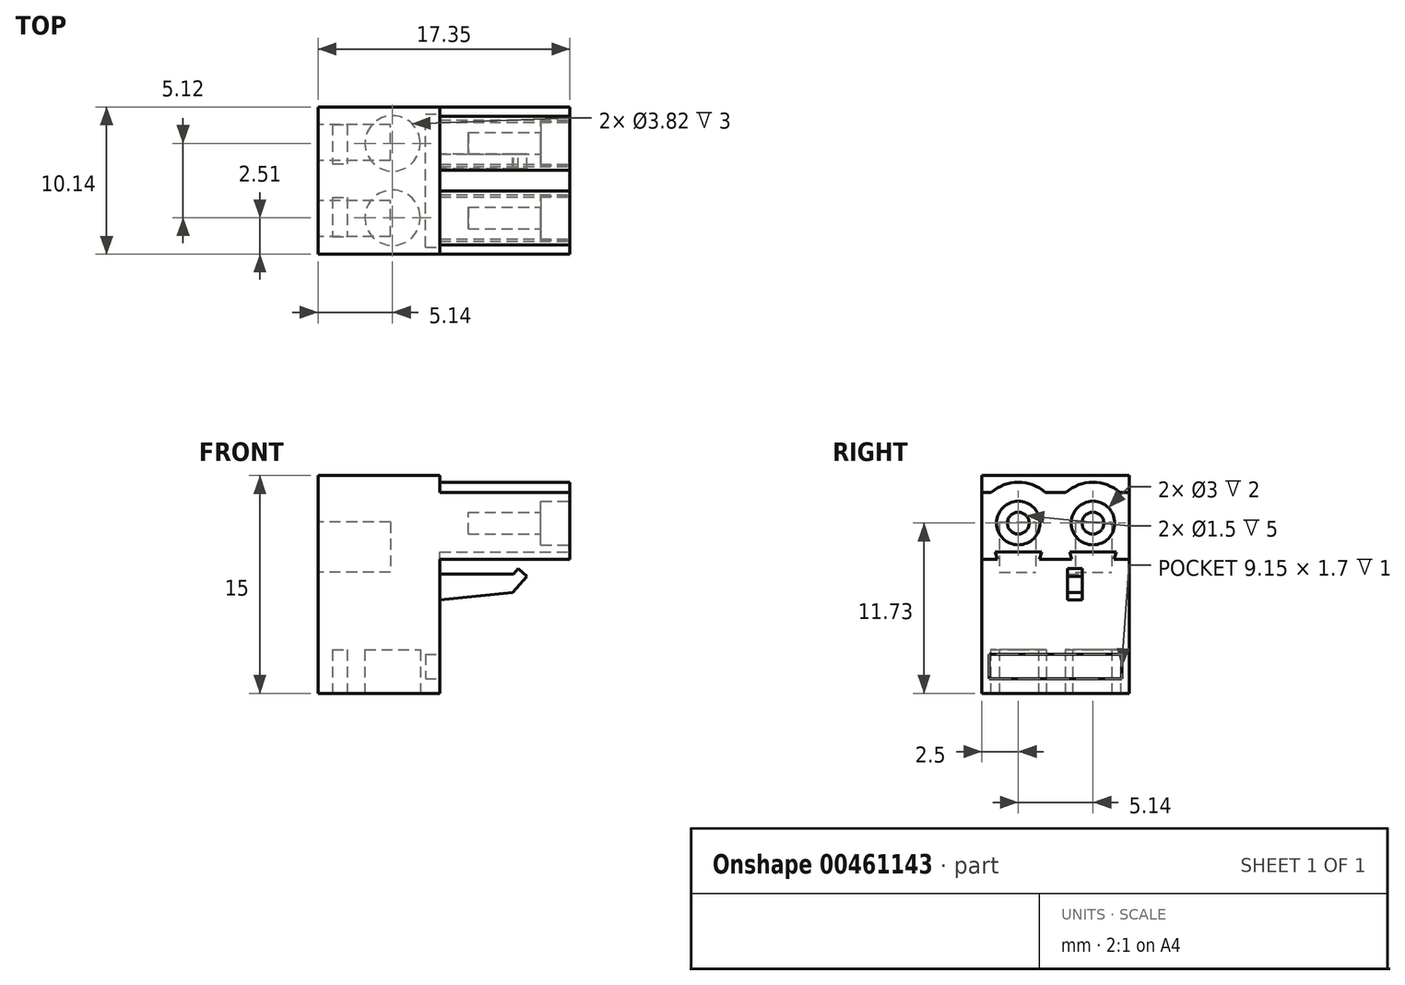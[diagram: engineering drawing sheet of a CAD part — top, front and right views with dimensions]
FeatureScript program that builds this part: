
annotation { "Feature Type Name" : "Feature", "Feature Type Description" : "" }
export const myFeature = defineFeature(function(context is Context, id is Id, definition is map)
    precondition{}
    {
        {
            var Q0;
            Q0=qCreatedBy(makeId("Front.planeOp"),FACE);
            var sketch = newSketch(context, id + "F0", { "sketchPlane" : qUnion([Q0])});
            skLineSegment(sketch, "E0", {"start": v(0, 15) * mm, "end": v(0, 0) * mm});
            skLineSegment(sketch, "E1", {"start": v(0, 0) * mm, "end": v(8.4, 0) * mm});
            skLineSegment(sketch, "E2", {"start": v(8.4, 0) * mm, "end": v(8.4, 9.23) * mm});
            skLineSegment(sketch, "E3", {"start": v(8.4, 9.23) * mm, "end": v(17.35, 9.23) * mm});
            skLineSegment(sketch, "E4", {"start": v(17.35, 9.23) * mm, "end": v(17.35, 13.83) * mm});
            skLineSegment(sketch, "E5", {"start": v(17.35, 13.83) * mm, "end": v(8.4, 13.83) * mm});
            skLineSegment(sketch, "E6", {"start": v(8.4, 13.83) * mm, "end": v(8.4, 15) * mm});
            skLineSegment(sketch, "E7", {"start": v(8.4, 15) * mm, "end": v(0, 15) * mm});
            skSolve(sketch);
        }
        {
            var Q0;
            Q0 = qSketchRegion(id + "F0", true);
            extrude(context, id + "F1", {"entities" : qUnion([Q0]), "depth" : 10.14 * mm});
        }
        {
            var Q0;
            Q0=makeQuery(id+"F1.opExtrude","SWEPT_FACE",FACE,{"disambiguationData":[OSD([sQuery(id+"F0.wireOp",EDGE,"E1")])]});
            var sketch = newSketch(context, id + "F2", { "sketchPlane" : qUnion([Q0])});
            skCircle(sketch, "E8", {"center": v(5.14, 2.5) * mm, "radius": 1.91 * mm});
            skCircle(sketch, "E9", {"center": v(5.14, 7.63) * mm, "radius": 1.91 * mm});
            skPoint(sketch, "E10", {"position": v(5.14, 9.54) * mm});
            skPoint(sketch, "E11", {"position": v(5.14, 0.6) * mm});
            skPoint(sketch, "E12", {"position": v(7.05, 2.5) * mm});
            skPoint(sketch, "E13", {"position": v(7.05, 7.63) * mm});
            skPoint(sketch, "E14", {"position": v(5.14, 4.42) * mm});
            skPoint(sketch, "E15", {"position": v(5.14, 5.72) * mm});
            skPoint(sketch, "E16", {"position": v(0, 0) * mm});
            skPoint(sketch, "E17", {"position": v(0, 10.14) * mm});
            skLineSegment(sketch, "E18.bottom", {"start": v(1, 1.2) * mm, "end": v(2, 1.2) * mm});
            skLineSegment(sketch, "E18.top", {"start": v(1, 3.9) * mm, "end": v(2, 3.9) * mm});
            skLineSegment(sketch, "E18.left", {"start": v(1, 1.2) * mm, "end": v(1, 3.9) * mm});
            skLineSegment(sketch, "E18.right", {"start": v(2, 1.2) * mm, "end": v(2, 3.9) * mm});
            skLineSegment(sketch, "E19.bottom", {"start": v(1, 6.24) * mm, "end": v(2, 6.24) * mm});
            skLineSegment(sketch, "E19.top", {"start": v(1, 8.94) * mm, "end": v(2, 8.94) * mm});
            skLineSegment(sketch, "E19.left", {"start": v(1, 6.24) * mm, "end": v(1, 8.94) * mm});
            skLineSegment(sketch, "E19.right", {"start": v(2, 6.24) * mm, "end": v(2, 8.94) * mm});
            skSolve(sketch);
        }
        {
            var Q0;
            Q0 = qSketchRegion(id + "F2", true);
            extrude(context, id + "F3", {"entities" : qUnion([Q0]), "operationType" : NewBodyOperationType.REMOVE, "oppositeDirection" : true, "depth" : 3 * mm});
        }
        {
            var Q0;
            Q0=makeQuery(id+"F1.opExtrude","SWEPT_FACE",FACE,{"disambiguationData":[OSD([sQuery(id+"F0.wireOp",EDGE,"E0")])]});
            var sketch = newSketch(context, id + "F4", { "sketchPlane" : qUnion([Q0])});
            skLineSegment(sketch, "E20.bottom", {"start": v(8.94, 11.8) * mm, "end": v(6.44, 11.8) * mm});
            skLineSegment(sketch, "E20.top", {"start": v(8.94, 8.35) * mm, "end": v(6.44, 8.35) * mm});
            skLineSegment(sketch, "E20.left", {"start": v(8.94, 11.8) * mm, "end": v(8.94, 8.35) * mm});
            skLineSegment(sketch, "E20.right", {"start": v(6.44, 11.8) * mm, "end": v(6.44, 8.35) * mm});
            skLineSegment(sketch, "E21.bottom", {"start": v(3.7, 11.8) * mm, "end": v(1.2, 11.8) * mm});
            skLineSegment(sketch, "E21.top", {"start": v(3.7, 8.35) * mm, "end": v(1.2, 8.35) * mm});
            skLineSegment(sketch, "E21.left", {"start": v(3.7, 11.8) * mm, "end": v(3.7, 8.35) * mm});
            skLineSegment(sketch, "E21.right", {"start": v(1.2, 11.8) * mm, "end": v(1.2, 8.35) * mm});
            skSolve(sketch);
        }
        {
            var Q0;
            Q0 = qSketchRegion(id + "F4", true);
            extrude(context, id + "F5", {"entities" : qUnion([Q0]), "operationType" : NewBodyOperationType.REMOVE, "oppositeDirection" : true, "depth" : 5 * mm});
        }
        {
            var Q0;
            Q0=makeQuery(id+"F1.opExtrude","SWEPT_FACE",FACE,{"disambiguationData":[OSD([sQuery(id+"F0.wireOp",EDGE,"E4")])]});
            var sketch = newSketch(context, id + "F6", { "sketchPlane" : qUnion([Q0])});
            skCircle(sketch, "E22", {"center": v(-2.5, 11.73) * mm, "radius": 1.5 * mm});
            skCircle(sketch, "E23", {"center": v(-7.64, 11.73) * mm, "radius": 1.5 * mm});
            skPoint(sketch, "E24", {"position": v(-2.5, 10.23) * mm});
            skPoint(sketch, "E25", {"position": v(-1, 11.73) * mm});
            skPoint(sketch, "E26", {"position": v(-6.14, 11.73) * mm});
            skPoint(sketch, "E27", {"position": v(-7.64, 10.23) * mm});
            skPoint(sketch, "E28", {"position": v(-9.14, 11.73) * mm});
            skSolve(sketch);
        }
        {
            var Q0;
            Q0 = qSketchRegion(id + "F6", true);
            extrude(context, id + "F7", {"entities" : qUnion([Q0]), "operationType" : NewBodyOperationType.REMOVE, "oppositeDirection" : true, "depth" : 2 * mm});
        }
        {
            var Q0;
            Q0=makeQuery(id+"F1.opExtrude","SWEPT_FACE",FACE,{"disambiguationData":[OSD([sQuery(id+"F0.wireOp",EDGE,"E4")])]});
            var sketch = newSketch(context, id + "F8", { "sketchPlane" : qUnion([Q0])});
            skLineSegment(sketch, "E29", {"start": v(-9.1, 9.23) * mm, "end": v(-9.25, 9.73) * mm});
            skLineSegment(sketch, "E30", {"start": v(-9.25, 9.73) * mm, "end": v(-6.03, 9.73) * mm});
            skLineSegment(sketch, "E31", {"start": v(-6.03, 9.73) * mm, "end": v(-6.2, 9.23) * mm});
            skLineSegment(sketch, "E32", {"start": v(-6.2, 9.23) * mm, "end": v(-9.1, 9.23) * mm});
            skLineSegment(sketch, "E33", {"start": v(-5.07, 9.23) * mm, "end": v(-5.07, 13.83) * mm, "construction": true});
            skLineSegment(sketch, "E34.MirrorCS", {"start": v(-0.9, 9.73) * mm, "end": v(-4.1, 9.73) * mm});
            skLineSegment(sketch, "E35.MirrorCS", {"start": v(-4.1, 9.73) * mm, "end": v(-3.95, 9.23) * mm});
            skLineSegment(sketch, "E36.MirrorCS", {"start": v(-3.95, 9.23) * mm, "end": v(-1.05, 9.23) * mm});
            skLineSegment(sketch, "E37.MirrorCS", {"start": v(-1.05, 9.23) * mm, "end": v(-0.9, 9.73) * mm});
            skPoint(sketch, "E38", {"position": v(-7.64, 9.23) * mm});
            skPoint(sketch, "E39", {"position": v(-7.64, 11.73) * mm});
            skLineSegment(sketch, "E40", {"start": v(-7.64, 11.73) * mm, "end": v(-7.64, 9.23) * mm});
            skSolve(sketch);
        }
        {
            var Q0;
            Q0 = qSketchRegion(id + "F8", true);
            extrude(context, id + "F9", {"entities" : qUnion([Q0]), "operationType" : NewBodyOperationType.REMOVE, "oppositeDirection" : true, "depth" : 8.95 * mm});
        }
        {
            var Q0;
            Q0=makeQuery(id+"F1.opExtrude","SWEPT_FACE",FACE,{"disambiguationData":[OSD([sQuery(id+"F0.wireOp",EDGE,"E4")])]});
            var sketch = newSketch(context, id + "F10", { "sketchPlane" : qUnion([Q0])});
            skPoint(sketch, "E41", {"position": v(-7.64, 11.73) * mm});
            skArc(sketch, "E42", {"start": v(-5.77, 13.83) * mm, "mid": v(-7.64, 14.54) * mm, "end": v(-9.5, 13.83) * mm});
            skLineSegment(sketch, "E43", {"start": v(-9.5, 13.83) * mm, "end": v(-5.77, 13.83) * mm});
            skPoint(sketch, "E44", {"position": v(-5.07, 13.83) * mm});
            skLineSegment(sketch, "E45", {"start": v(-5.07, 13.83) * mm, "end": v(-5.07, 9.23) * mm, "construction": true});
            skArc(sketch, "E46.MirrorCS", {"start": v(-4.37, 13.83) * mm, "mid": v(-2.5, 14.54) * mm, "end": v(-0.63, 13.83) * mm});
            skLineSegment(sketch, "E47.MirrorCS", {"start": v(-0.63, 13.83) * mm, "end": v(-4.37, 13.83) * mm});
            skSolve(sketch);
        }
        {
            var Q0;
            Q0 = qSketchRegion(id + "F10", true);
            extrude(context, id + "F11", {"entities" : qUnion([Q0]), "operationType" : NewBodyOperationType.ADD, "endBound" : BoundingType.UP_TO_NEXT, "oppositeDirection" : true, "depth" : 25 * mm});
        }
        {
            var Q0;
            Q0=makeQuery(id+"F7.boolean.opBoolean","COPY",FACE,{"derivedFrom":makeQuery(id+"F7.opExtrude","CAP_FACE",FACE,{"disambiguationData":[OSD([sQuery(id+"F6.wireOp",EDGE,"E23")])],"isStart":false})});
            var sketch = newSketch(context, id + "F12", { "sketchPlane" : qUnion([Q0])});
            skCircle(sketch, "E48", {"center": v(-7.64, 11.73) * mm, "radius": 0.75 * mm});
            skSolve(sketch);
        }
        {
            var Q0;
            Q0 = qSketchRegion(id + "F12", true);
            extrude(context, id + "F13", {"entities" : qUnion([Q0]), "operationType" : NewBodyOperationType.REMOVE, "oppositeDirection" : true, "depth" : 5 * mm});
        }
        {
            var Q0;
            Q0=makeQuery(id+"F7.boolean.opBoolean","COPY",FACE,{"derivedFrom":makeQuery(id+"F7.opExtrude","CAP_FACE",FACE,{"disambiguationData":[OSD([sQuery(id+"F6.wireOp",EDGE,"E22")])],"isStart":false})});
            var sketch = newSketch(context, id + "F14", { "sketchPlane" : qUnion([Q0])});
            skCircle(sketch, "E49", {"center": v(-2.5, 11.73) * mm, "radius": 0.75 * mm});
            skSolve(sketch);
        }
        {
            var Q0;
            Q0 = qSketchRegion(id + "F14", true);
            extrude(context, id + "F15", {"entities" : qUnion([Q0]), "operationType" : NewBodyOperationType.REMOVE, "oppositeDirection" : true, "depth" : 5 * mm});
        }
        {
            var Q0;
            Q0=makeQuery(id+"F9.boolean.opBoolean","MERGE",FACE,{"derivedFrom":[makeQuery(id+"F1.opExtrude","SWEPT_FACE",FACE,{"disambiguationData":[OSD([sQuery(id+"F0.wireOp",EDGE,"E2")])]}),makeQuery(id+"F9.opExtrude","CAP_FACE",FACE,{"disambiguationData":[OSD([sQuery(id+"F8.wireOp",EDGE,"E29"),sQuery(id+"F8.wireOp",EDGE,"E30"),sQuery(id+"F8.wireOp",EDGE,"E31"),sQuery(id+"F8.wireOp",EDGE,"E32")])],"isStart":false}),makeQuery(id+"F9.opExtrude","CAP_FACE",FACE,{"disambiguationData":[OSD([sQuery(id+"F8.wireOp",EDGE,"E34.MirrorCS"),sQuery(id+"F8.wireOp",EDGE,"E35.MirrorCS"),sQuery(id+"F8.wireOp",EDGE,"E36.MirrorCS"),sQuery(id+"F8.wireOp",EDGE,"E37.MirrorCS")])],"isStart":false})]});
            var sketch = newSketch(context, id + "F16", { "sketchPlane" : qUnion([Q0])});
            skLineSegment(sketch, "E50.bottom", {"start": v(-9.65, 2.7) * mm, "end": v(-0.5, 2.7) * mm});
            skLineSegment(sketch, "E50.top", {"start": v(-9.65, 1) * mm, "end": v(-0.5, 1) * mm});
            skLineSegment(sketch, "E50.left", {"start": v(-9.65, 2.7) * mm, "end": v(-9.65, 1) * mm});
            skLineSegment(sketch, "E50.right", {"start": v(-0.5, 2.7) * mm, "end": v(-0.5, 1) * mm});
            skPoint(sketch, "E51", {"position": v(-5.07, 2.7) * mm});
            skLineSegment(sketch, "E52", {"start": v(-5.07, 0) * mm, "end": v(-5.07, 5.28) * mm, "construction": true});
            skSolve(sketch);
        }
        {
            var Q0;
            Q0 = qSketchRegion(id + "F16", true);
            extrude(context, id + "F17", {"entities" : qUnion([Q0]), "operationType" : NewBodyOperationType.REMOVE, "oppositeDirection" : true, "depth" : 1 * mm});
        }
        {
            var Q0;
            Q0=makeQuery(id+"F1.opExtrude","CAP_FACE",FACE,{"disambiguationData":[OSD([sQuery(id+"F0.wireOp",EDGE,"E0"),sQuery(id+"F0.wireOp",EDGE,"E1"),sQuery(id+"F0.wireOp",EDGE,"E2"),sQuery(id+"F0.wireOp",EDGE,"E3"),sQuery(id+"F0.wireOp",EDGE,"E4"),sQuery(id+"F0.wireOp",EDGE,"E5"),sQuery(id+"F0.wireOp",EDGE,"E6"),sQuery(id+"F0.wireOp",EDGE,"E7")])],"isStart":true});
            cPlane(context, id + "F18", {"entities" : qUnion([Q0]), "cplaneType" : CPlaneType.OFFSET, "offset" : 3.25 * mm, "oppositeDirection" : true, "width" : 150 * mm, "height" : 150 * mm});
        }
        {
            var Q0;
            Q0=qCreatedBy(id+"F18.planeOp",FACE);
            var sketch = newSketch(context, id + "F19", { "sketchPlane" : qUnion([Q0])});
            skLineSegment(sketch, "E53", {"start": v(-8.4, 8.23) * mm, "end": v(-8.4, 6.43) * mm});
            skLineSegment(sketch, "E54", {"start": v(-8.4, 6.43) * mm, "end": v(-13.4, 6.95) * mm});
            skLineSegment(sketch, "E55", {"start": v(-13.4, 6.95) * mm, "end": v(-14.4, 8.07) * mm});
            skLineSegment(sketch, "E56", {"start": v(-14.4, 8.07) * mm, "end": v(-13.8, 8.6) * mm});
            skLineSegment(sketch, "E57", {"start": v(-13.8, 8.6) * mm, "end": v(-13.47, 8.23) * mm});
            skLineSegment(sketch, "E58", {"start": v(-13.47, 8.23) * mm, "end": v(-8.4, 8.23) * mm});
            skSolve(sketch);
        }
        {
            var Q0;
            Q0 = qSketchRegion(id + "F19", true);
            extrude(context, id + "F20", {"entities" : qUnion([Q0]), "operationType" : NewBodyOperationType.ADD, "oppositeDirection" : true, "depth" : 1 * mm});
        }
    });
